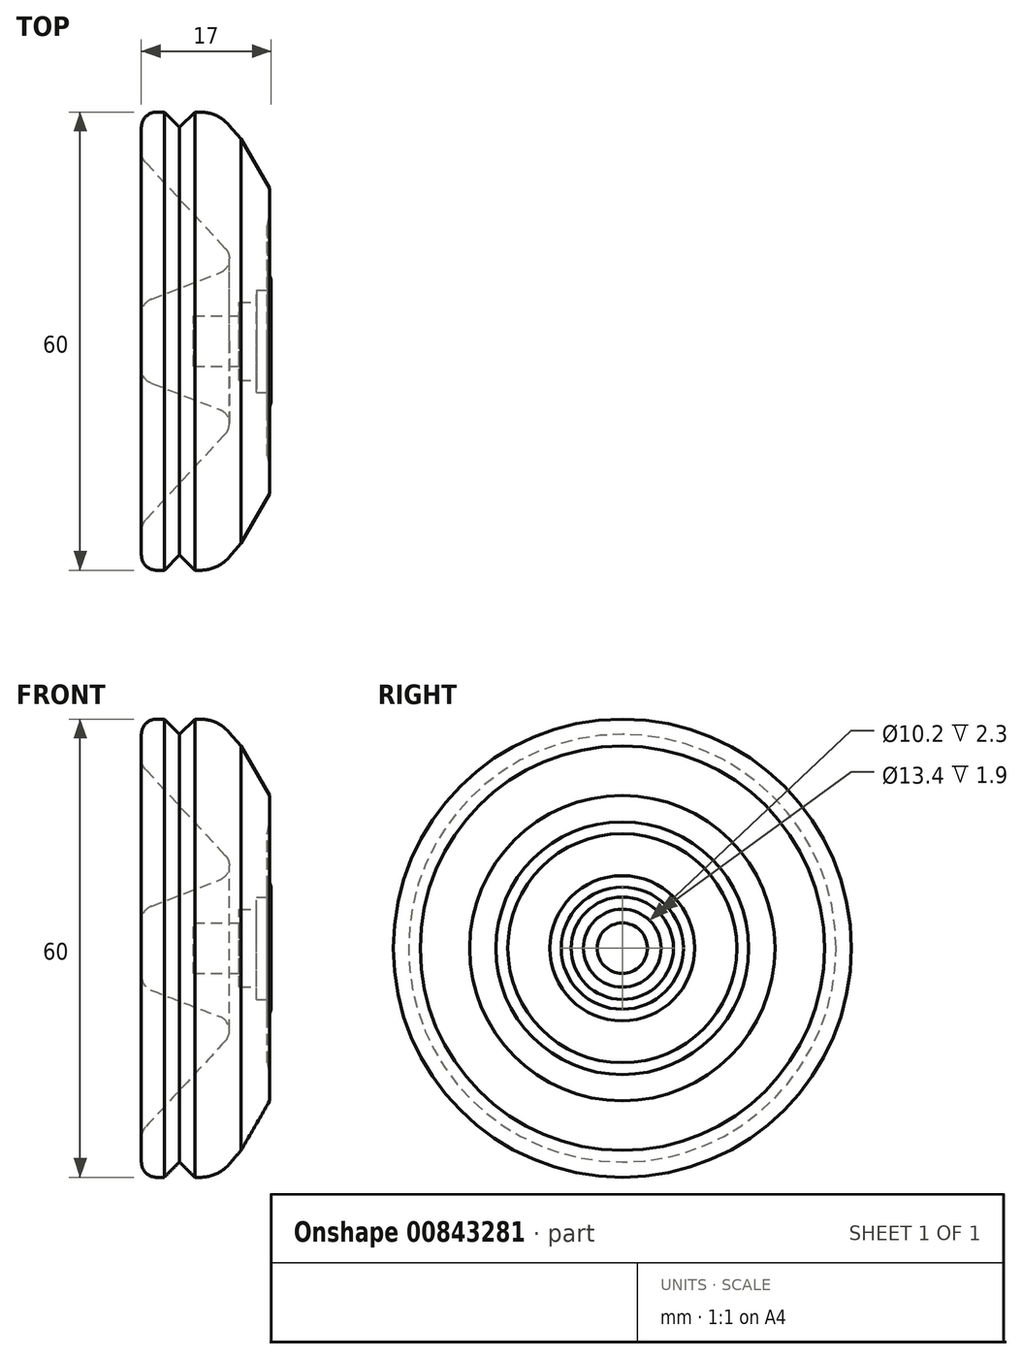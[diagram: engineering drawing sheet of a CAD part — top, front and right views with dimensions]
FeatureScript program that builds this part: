
annotation { "Feature Type Name" : "Feature", "Feature Type Description" : "" }
export const myFeature = defineFeature(function(context is Context, id is Id, definition is map)
    precondition{}
    {
        {
            var Q0;
            Q0=qCreatedBy(makeId("Front.planeOp"),FACE);
            var sketch = newSketch(context, id + "F0", { "sketchPlane" : qUnion([Q0])});
            skLineSegment(sketch, "E0", {"start": v(0, 0) * mm, "end": v(0, 3.63) * mm});
            skLineSegment(sketch, "E1", {"start": v(1.28, 5.5) * mm, "end": v(10.24, 8.94) * mm});
            skLineSegment(sketch, "E2", {"start": v(10.99, 12.17) * mm, "end": v(0.53, 23.42) * mm});
            skLineSegment(sketch, "E3", {"start": v(0, 24.79) * mm, "end": v(0, 28) * mm});
            skLineSegment(sketch, "E4", {"start": v(2, 30) * mm, "end": v(3, 30) * mm});
            skLineSegment(sketch, "E5", {"start": v(3, 30) * mm, "end": v(5, 28) * mm});
            skLineSegment(sketch, "E6", {"start": v(5, 28) * mm, "end": v(7, 30) * mm});
            skLineSegment(sketch, "E7", {"start": v(16.8, 20) * mm, "end": v(16.8, 16.55) * mm});
            skLineSegment(sketch, "E8", {"start": v(16.8, 16.55) * mm, "end": v(16.5, 15) * mm});
            skLineSegment(sketch, "E9", {"start": v(16.5, 15) * mm, "end": v(16.5, 9.5) * mm});
            skLineSegment(sketch, "E10", {"start": v(16.5, 9.5) * mm, "end": v(17, 8) * mm});
            skLineSegment(sketch, "E11", {"start": v(17, 8) * mm, "end": v(17, 6.7) * mm});
            skLineSegment(sketch, "E12", {"start": v(17, 6.7) * mm, "end": v(15.1, 6.7) * mm});
            skLineSegment(sketch, "E13", {"start": v(15.1, 6.7) * mm, "end": v(15.1, 5.1) * mm});
            skLineSegment(sketch, "E14", {"start": v(15.1, 5.1) * mm, "end": v(12.8, 5.1) * mm});
            skLineSegment(sketch, "E15", {"start": v(12.8, 5.1) * mm, "end": v(12.8, 3.3) * mm});
            skLineSegment(sketch, "E16", {"start": v(12.8, 3.3) * mm, "end": v(6.8, 3.3) * mm});
            skLineSegment(sketch, "E17", {"start": v(6.8, 3.3) * mm, "end": v(6.8, 0) * mm});
            skLineSegment(sketch, "E18", {"start": v(6.8, 0) * mm, "end": v(0, 0) * mm});
            skLineSegment(sketch, "E19", {"start": v(7, 30) * mm, "end": v(7.72, 30) * mm});
            skLineSegment(sketch, "E20", {"start": v(11.5, 28.28) * mm, "end": v(13.06, 26.48) * mm});
            skLineSegment(sketch, "E21", {"start": v(13.06, 26.48) * mm, "end": v(16.8, 20) * mm});
            skPoint(sketch, "E22.visualSharp", {"position": v(0, 30) * mm});
            skArc(sketch, "E22.filletArc", {"start": v(2, 30) * mm, "mid": v(0.59, 29.41) * mm, "end": v(0, 28) * mm});
            skPoint(sketch, "E23.visualSharp", {"position": v(10, 30) * mm});
            skArc(sketch, "E23.filletArc", {"start": v(11.5, 28.28) * mm, "mid": v(9.8, 29.55) * mm, "end": v(7.72, 30) * mm});
            skPoint(sketch, "E24.visualSharp", {"position": v(0, 24) * mm});
            skArc(sketch, "E24.filletArc", {"start": v(0, 24.79) * mm, "mid": v(0.14, 24.05) * mm, "end": v(0.53, 23.42) * mm});
            skPoint(sketch, "E25.visualSharp", {"position": v(0, 5) * mm});
            skArc(sketch, "E25.filletArc", {"start": v(1.28, 5.5) * mm, "mid": v(0.35, 4.76) * mm, "end": v(0, 3.63) * mm});
            skPoint(sketch, "E26.visualSharp", {"position": v(13, 10) * mm});
            skArc(sketch, "E26.filletArc", {"start": v(10.24, 8.94) * mm, "mid": v(11.47, 10.35) * mm, "end": v(10.99, 12.17) * mm});
            skSolve(sketch);
        }
        {
            var Q0;
            Q0=makeQuery(id+"F0.imprint","IMPRINT",FACE,{"disambiguationData":[TD([[makeQuery(id+"F0.imprint","IMPRINT",EDGE,{"derivedFrom":sQuery(id+"F0.wireOp",EDGE,"E0")}),-1.0]])]});
            var Q1;
            Q1=sQuery(id+"F0.wireOp",EDGE,"E18");
            revolve(context, id + "F1", {"surfaceOperationType" : NewSurfaceOperationType.NEW, "entities" : qUnion([Q0]), "axis" : qUnion([Q1]), "revolveType" : RevolveType.FULL});
        }
    });
